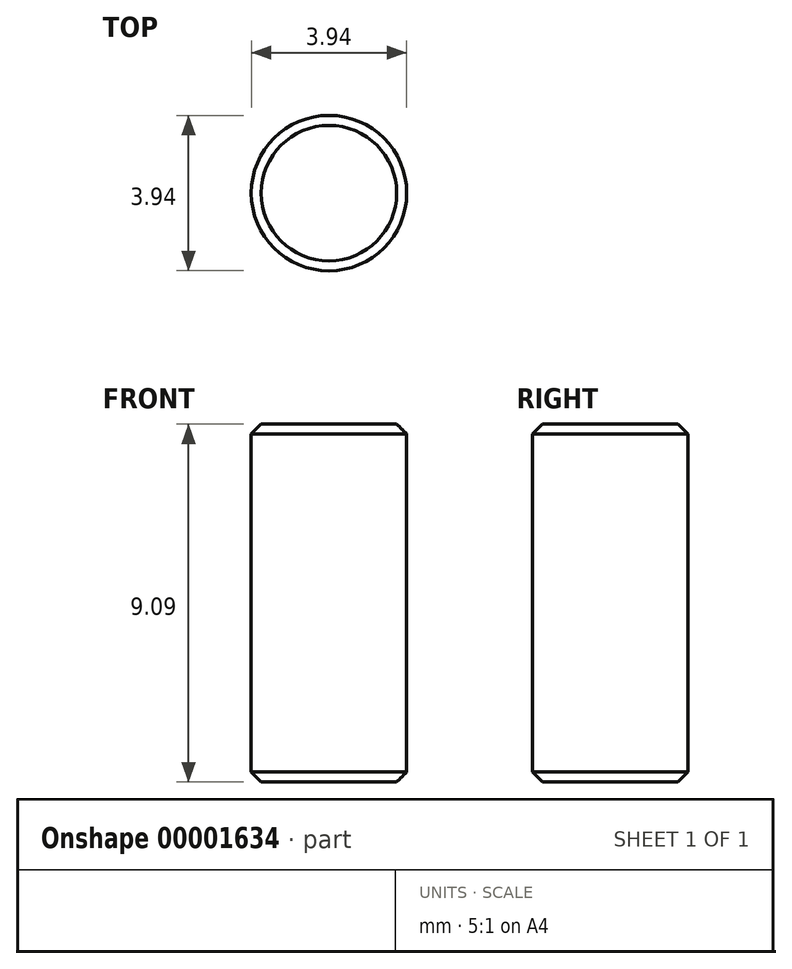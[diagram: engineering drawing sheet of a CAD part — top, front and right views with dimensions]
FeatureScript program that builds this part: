
annotation { "Feature Type Name" : "Feature", "Feature Type Description" : "" }
export const myFeature = defineFeature(function(context is Context, id is Id, definition is map)
    precondition{}
    {
        {
            var Q0;
            Q0=qCreatedBy(makeId("Top.planeOp"),FACE);
            var sketch = newSketch(context, id + "F0", { "sketchPlane" : qUnion([Q0])});
            skCircle(sketch, "E0", {"center": v(0, 0) * mm, "radius": 1.97 * mm});
            skSolve(sketch);
        }
        {
            var Q0;
            Q0=makeQuery(id+"F0.imprint","IMPRINT",FACE,{"disambiguationData":[TD([[makeQuery(id+"F0.imprint","IMPRINT",EDGE,{"derivedFrom":sQuery(id+"F0.wireOp",EDGE,"E0")}),1.0]])]});
            extrude(context, id + "F1", {"entities" : qUnion([Q0]), "depth" : 9.1 * mm});
        }
        {
            var Q0;
            Q0=makeQuery(id+"F1.opExtrude","CAP_EDGE",EDGE,{"disambiguationData":[OSD([sQuery(id+"F0.wireOp",EDGE,"E0")])],"isStart":false});
            var Q1;
            Q1=makeQuery(id+"F1.opExtrude","CAP_EDGE",EDGE,{"disambiguationData":[OSD([sQuery(id+"F0.wireOp",EDGE,"E0")])],"isStart":true});
            chamfer(context, id + "F2", {"entities" : qUnion([Q0, Q1]), "width" : 0.25 * mm, "tangentPropagation" : true});
        }
    });
